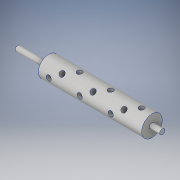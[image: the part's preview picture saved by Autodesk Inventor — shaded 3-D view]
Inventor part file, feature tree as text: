
AUTODESK INVENTOR PART (.ipt)
format: ipt  version: 2019 (Build 230136000, 136)  size: 162,304 bytes
history: native  units: in
note: dims shown in document units (in); Inventor stores cm internally (conversion verified against a paired STEP export)
features: sketch x5, plane x4, hole x3, revolve x1, pattern_linear x1, extrude x1, projected_geometry x1
ambient origin geometry x8: Origin, YZ Plane, XZ Plane, XY Plane, X Axis, Y Axis, Z Axis, Center Point
bodies: Solid1 (feature_tree)
feature tree (16):
  revolve  "Revolution1"  [1 undecoded]
  plane  "Work Plane1"
  hole  "Hole1"  [1 undecoded]
  plane  "Work Plane3"
  hole  "Hole2"  [1 undecoded]
  plane  "Work Plane4"
  hole  "Hole3"  [1 undecoded]
  pattern_linear  "Rectangular Pattern1"  Spacing1=1.0in  [1 undecoded]
  extrude  "Extrusion1"  Depth=1.5in
  sketch  "Sketch1"  dims[d0=0.25in d1=1.0in]
  sketch  "Sketch2"  dims[d2=1.5in d3=1.5in]
  plane  "Work Plane2"
  sketch  "Sketch3"  dims[d4=5.0in d5=90.0deg]
  sketch  "Sketch4"  dims[d6=0.5in]
  sketch  "Sketch5"  dims[d7=0.25in d8=0.75in d9=0.375in d10=0.25in d11=0.5635in d12=0.75in d13=0.8108in d14=45.0deg d15=1.0in d16=0.25in d17=0.75in d18=0.375in d19=0.25in d20=0.5635in d21=0.75in d22=0.8108in d23=1.5in d24=0.25in d25=0.75in d26=0.375in d27=0.25in d28=0.5635in d29=0.75in d30=0.8108in d31=1.1811in d33=1.5in d34=1.0in d35=0.0in]
  projected_geometry  "Projected Loop1"
note: 5 required parameter values undecoded (feature->parameter linkage not recoverable at this tier; creation-order binding heuristic only, values carry confidence <= 0.55)